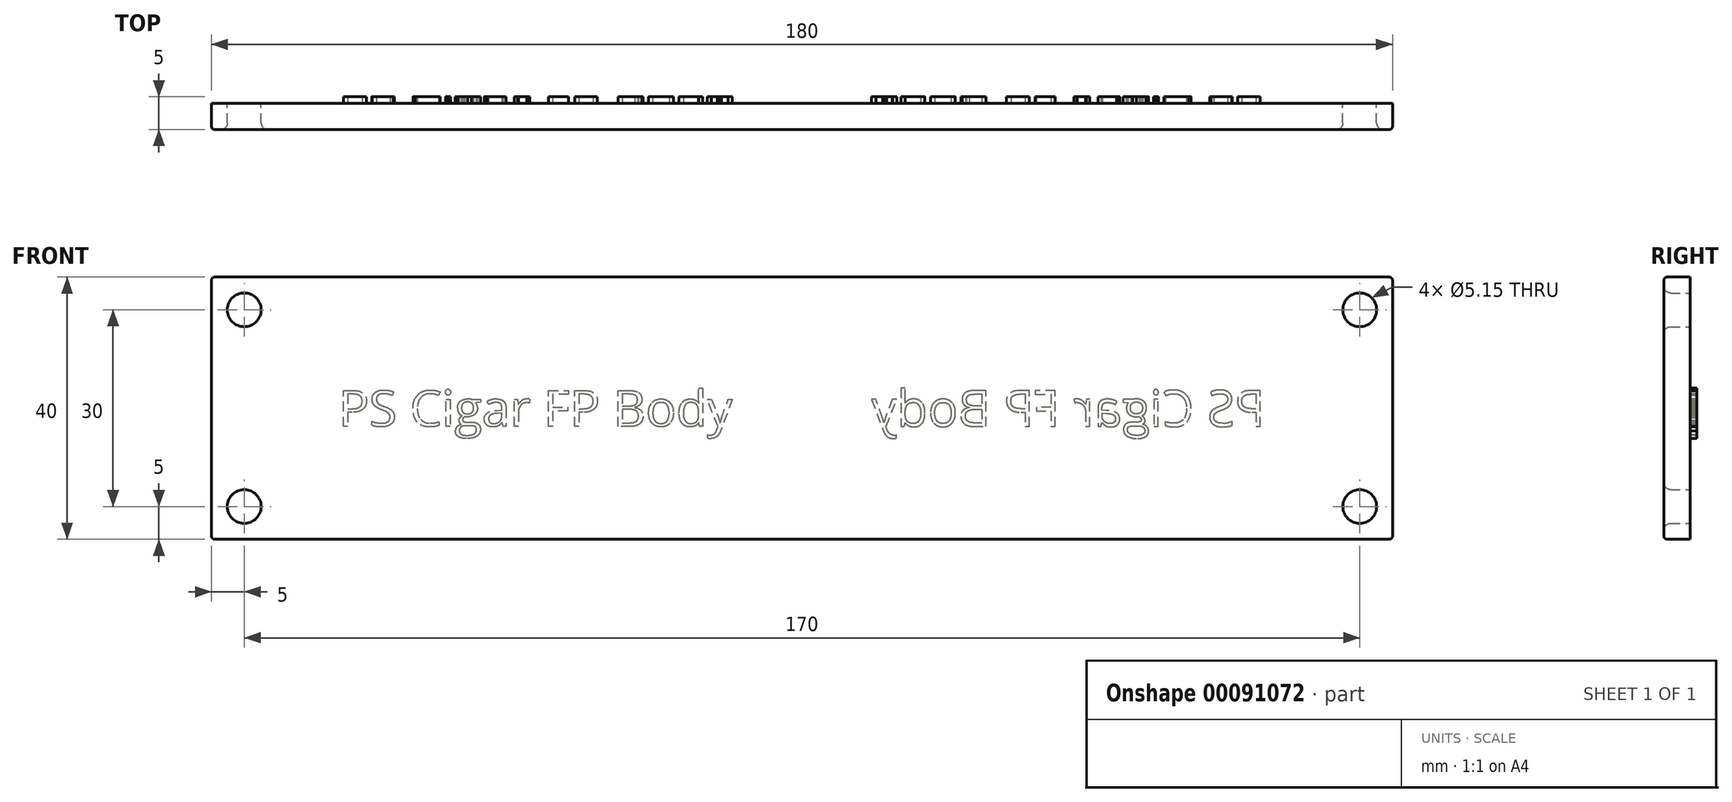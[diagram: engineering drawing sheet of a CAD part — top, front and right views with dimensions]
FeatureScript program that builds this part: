
annotation { "Feature Type Name" : "Feature", "Feature Type Description" : "" }
export const myFeature = defineFeature(function(context is Context, id is Id, definition is map)
    precondition{}
    {
        {
            var Q0;
            Q0=qCreatedBy(makeId("Front.planeOp"),FACE);
            var sketch = newSketch(context, id + "F0", { "sketchPlane" : qUnion([Q0])});
            skLineSegment(sketch, "E0.bottom", {"start": v(-90, -20) * mm, "end": v(90, -20) * mm});
            skLineSegment(sketch, "E0.top", {"start": v(-90, 20) * mm, "end": v(90, 20) * mm});
            skLineSegment(sketch, "E0.left", {"start": v(-90, -20) * mm, "end": v(-90, 20) * mm});
            skLineSegment(sketch, "E0.right", {"start": v(90, -20) * mm, "end": v(90, 20) * mm});
            skPoint(sketch, "E0.middle", {"position": v(0, 0) * mm});
            skCircle(sketch, "E1", {"center": v(-85, 15) * mm, "radius": 2.58 * mm});
            skPoint(sketch, "E2.start.orphan", {"position": v(-90, 0) * mm});
            skPoint(sketch, "E3.orphan", {"position": v(0, 20) * mm});
            skPoint(sketch, "E4.end.orphan", {"position": v(0, -20) * mm});
            skLineSegment(sketch, "E5", {"start": v(-90, 0) * mm, "end": v(0, 0) * mm, "construction": true});
            skLineSegment(sketch, "E6", {"start": v(0, 20) * mm, "end": v(0, -20) * mm, "construction": true});
            skCircle(sketch, "E7.MirrorC", {"center": v(-85, -15) * mm, "radius": 2.58 * mm});
            skCircle(sketch, "E8.MirrorC", {"center": v(85, 15) * mm, "radius": 2.58 * mm});
            skCircle(sketch, "E9.MirrorC", {"center": v(85, -15) * mm, "radius": 2.58 * mm});
            skSolve(sketch);
        }
        {
            var Q0;
            Q0=makeQuery(id+"F0.imprint","IMPRINT",FACE,{"disambiguationData":[TD([[makeQuery(id+"F0.imprint","IMPRINT",EDGE,{"derivedFrom":sQuery(id+"F0.wireOp",EDGE,"E0.bottom")}),1.0]])]});
            extrude(context, id + "F1", {"entities" : qUnion([Q0]), "depth" : 4 * mm});
        }
        {
            var Q0;
            Q0=makeQuery(id+"F1.opExtrude","CAP_EDGE",EDGE,{"disambiguationData":[OSD([sQuery(id+"F0.wireOp",EDGE,"E1")])],"isStart":false});
            var Q1;
            Q1=makeQuery(id+"F1.opExtrude","CAP_EDGE",EDGE,{"disambiguationData":[OSD([sQuery(id+"F0.wireOp",EDGE,"f5b72a5b-8583-449a-bdbf-9ac5a681e1fd0.MirrorC")])],"isStart":false});
            var Q2;
            Q2=makeQuery(id+"F1.opExtrude","CAP_EDGE",EDGE,{"disambiguationData":[OSD([sQuery(id+"F0.wireOp",EDGE,"2623e306-60f4-4522-aa65-1e3e8c2cf5b60.MirrorC")])],"isStart":false});
            var Q3;
            Q3=makeQuery(id+"F1.opExtrude","CAP_EDGE",EDGE,{"disambiguationData":[OSD([sQuery(id+"F0.wireOp",EDGE,"be81a34d-1d50-4ce7-a7a8-4484a1701fac0.MirrorC")])],"isStart":false});
            var Q4;
            Q4=makeQuery(id+"F1.opExtrude","CAP_EDGE",EDGE,{"disambiguationData":[OSD([sQuery(id+"F0.wireOp",EDGE,"E7.MirrorC")])],"isStart":false});
            var Q5;
            Q5=makeQuery(id+"F1.opExtrude","CAP_EDGE",EDGE,{"disambiguationData":[OSD([sQuery(id+"F0.wireOp",EDGE,"E8.MirrorC")])],"isStart":false});
            var Q6;
            Q6=makeQuery(id+"F1.opExtrude","CAP_EDGE",EDGE,{"disambiguationData":[OSD([sQuery(id+"F0.wireOp",EDGE,"E9.MirrorC")])],"isStart":false});
            fillet(context, id + "F2", {"entities" : qUnion([Q0, Q1, Q2, Q3, Q4, Q5, Q6]), "radius" : 1 * mm, "tangentPropagation" : true, "allowEdgeOverflow" : false});
        }
        {
            var Q0;
            Q0=makeQuery(id+"F1.opExtrude","CAP_EDGE",EDGE,{"disambiguationData":[OSD([sQuery(id+"F0.wireOp",EDGE,"E0.top")])],"isStart":false});
            var Q1;
            Q1=makeQuery(id+"F1.opExtrude","CAP_EDGE",EDGE,{"disambiguationData":[OSD([sQuery(id+"F0.wireOp",EDGE,"E0.left")])],"isStart":false});
            var Q2;
            Q2=makeQuery(id+"F1.opExtrude","CAP_EDGE",EDGE,{"disambiguationData":[OSD([sQuery(id+"F0.wireOp",EDGE,"E0.bottom")])],"isStart":false});
            var Q3;
            Q3=makeQuery(id+"F1.opExtrude","CAP_EDGE",EDGE,{"disambiguationData":[OSD([sQuery(id+"F0.wireOp",EDGE,"E0.right")])],"isStart":false});
            var Q4;
            Q4=makeQuery(id+"F1.opExtrude","SWEPT_EDGE",EDGE,{"disambiguationData":[OSD([sQuery(id+"F0.wireOp",EDGE,"E0.top"),sQuery(id+"F0.wireOp",EDGE,"E0.left")])]});
            var Q5;
            Q5=makeQuery(id+"F1.opExtrude","SWEPT_EDGE",EDGE,{"disambiguationData":[OSD([sQuery(id+"F0.wireOp",EDGE,"E0.bottom"),sQuery(id+"F0.wireOp",EDGE,"E0.left")])]});
            var Q6;
            Q6=makeQuery(id+"F1.opExtrude","SWEPT_EDGE",EDGE,{"disambiguationData":[OSD([sQuery(id+"F0.wireOp",EDGE,"E0.top"),sQuery(id+"F0.wireOp",EDGE,"E0.right")])]});
            var Q7;
            Q7=makeQuery(id+"F1.opExtrude","SWEPT_EDGE",EDGE,{"disambiguationData":[OSD([sQuery(id+"F0.wireOp",EDGE,"E0.bottom"),sQuery(id+"F0.wireOp",EDGE,"E0.right")])]});
            fillet(context, id + "F3", {"entities" : qUnion([Q0, Q1, Q2, Q3, Q4, Q5, Q6, Q7]), "radius" : .5 * mm, "tangentPropagation" : true, "allowEdgeOverflow" : false});
        }
        {
            var Q0;
            Q0=makeQuery(id+"F1.opExtrude","CAP_FACE",FACE,{"disambiguationData":[OSD([sQuery(id+"F0.wireOp",EDGE,"E0.bottom"),sQuery(id+"F0.wireOp",EDGE,"E0.top"),sQuery(id+"F0.wireOp",EDGE,"E0.left"),sQuery(id+"F0.wireOp",EDGE,"E0.right"),sQuery(id+"F0.wireOp",EDGE,"E1"),sQuery(id+"F0.wireOp",EDGE,"E7.MirrorC"),sQuery(id+"F0.wireOp",EDGE,"E8.MirrorC"),sQuery(id+"F0.wireOp",EDGE,"E9.MirrorC")])],"isStart":true});
            var sketch = newSketch(context, id + "F4", { "sketchPlane" : qUnion([Q0])});
            skText(sketch, "E10", { "text": "PS Cigar FP Body", "fontName": "OpenSans-Regular.ttf"});
            skLineSegment(sketch, "E11", {"start": v(0, 20) * mm, "end": v(0, -20) * mm, "construction": true});
            const initialGuessF4  = {"E10": [-0.0706, -0.00278, 1, 0, 0.00553]};
            skSetInitialGuess(sketch, initialGuessF4);
            skSolve(sketch);
        }
        {
            var Q0;
            Q0=qSketchRegion(id+"F4",true);
            extrude(context, id + "F5", {"entities" : qUnion([Q0]), "operationType" : NewBodyOperationType.ADD, "depth" : 1 * mm});
        }
        {
            var Q0;
            Q0=makeQuery(id+"F1.opExtrude","SWEPT_BODY",BODY,{"disambiguationData":[OSD([sQuery(id+"F0.wireOp",EDGE,"E0.bottom"),sQuery(id+"F0.wireOp",EDGE,"E0.top"),sQuery(id+"F0.wireOp",EDGE,"E0.left"),sQuery(id+"F0.wireOp",EDGE,"E0.right"),sQuery(id+"F0.wireOp",EDGE,"E1"),sQuery(id+"F0.wireOp",EDGE,"E7.MirrorC"),sQuery(id+"F0.wireOp",EDGE,"E8.MirrorC"),sQuery(id+"F0.wireOp",EDGE,"E9.MirrorC")])]});
            var Q1;
            Q1=makeQuery(id+"F5.opExtrude","SWEPT_FACE",FACE,{"disambiguationData":[OSD([sQuery(id+"F4.wireOp",EDGE,"E10.sketch_text.stroke-94")])]});
            var Q2;
            Q2=makeQuery(id+"F5.opExtrude","SWEPT_FACE",FACE,{"disambiguationData":[OSD([sQuery(id+"F4.wireOp",EDGE,"E10.sketch_text.stroke-169")])]});
            var Q3;
            Q3=makeQuery(id+"F5.opExtrude","SWEPT_FACE",FACE,{"disambiguationData":[OSD([sQuery(id+"F4.wireOp",EDGE,"E10.sketch_text.stroke-185")])]});
            var Q4;
            Q4=makeQuery(id+"F5.opExtrude","SWEPT_FACE",FACE,{"disambiguationData":[OSD([sQuery(id+"F4.wireOp",EDGE,"E10.sketch_text.stroke-125")])]});
            var Q5;
            Q5=makeQuery(id+"F5.opExtrude","SWEPT_FACE",FACE,{"disambiguationData":[OSD([sQuery(id+"F4.wireOp",EDGE,"E10.sketch_text.stroke-155")])]});
            var Q6;
            Q6=makeQuery(id+"F5.opExtrude","SWEPT_FACE",FACE,{"disambiguationData":[OSD([sQuery(id+"F4.wireOp",EDGE,"E10.sketch_text.stroke-65")])]});
            var Q7;
            Q7=makeQuery(id+"F5.opExtrude","SWEPT_FACE",FACE,{"disambiguationData":[OSD([sQuery(id+"F4.wireOp",EDGE,"E10.sketch_text.stroke-81")])]});
            var Q8;
            Q8=makeQuery(id+"F5.opExtrude","SWEPT_FACE",FACE,{"disambiguationData":[OSD([sQuery(id+"F4.wireOp",EDGE,"E10.sketch_text.stroke-67")])]});
            var Q9;
            Q9=makeQuery(id+"F5.opExtrude","SWEPT_FACE",FACE,{"disambiguationData":[OSD([sQuery(id+"F4.wireOp",EDGE,"E10.sketch_text.stroke-99")])]});
            var Q10;
            Q10=makeQuery(id+"F5.opExtrude","SWEPT_FACE",FACE,{"disambiguationData":[OSD([sQuery(id+"F4.wireOp",EDGE,"E10.sketch_text.stroke-127")])]});
            var Q11;
            Q11=makeQuery(id+"F5.opExtrude","SWEPT_FACE",FACE,{"disambiguationData":[OSD([sQuery(id+"F4.wireOp",EDGE,"E10.sketch_text.stroke-10")])]});
            var Q12;
            Q12=makeQuery(id+"F5.opExtrude","CAP_FACE",FACE,{"disambiguationData":[OSD([sQuery(id+"F4.wireOp",EDGE,"E10.sketch_text.stroke-9"),sQuery(id+"F4.wireOp",EDGE,"E10.sketch_text.stroke-10"),sQuery(id+"F4.wireOp",EDGE,"E10.sketch_text.stroke-11"),sQuery(id+"F4.wireOp",EDGE,"E10.sketch_text.stroke-12")])],"isStart":false});
            var Q13;
            Q13=makeQuery(id+"F5.opExtrude","SWEPT_FACE",FACE,{"disambiguationData":[OSD([sQuery(id+"F4.wireOp",EDGE,"E10.sketch_text.stroke-154")])]});
            var Q14;
            Q14=makeQuery(id+"F5.opExtrude","SWEPT_FACE",FACE,{"disambiguationData":[OSD([sQuery(id+"F4.wireOp",EDGE,"E10.sketch_text.stroke-1")])]});
            var Q15;
            Q15=makeQuery(id+"F5.opExtrude","CAP_FACE",FACE,{"disambiguationData":[OSD([sQuery(id+"F4.wireOp",EDGE,"E10.sketch_text.stroke-124"),sQuery(id+"F4.wireOp",EDGE,"E10.sketch_text.stroke-125"),sQuery(id+"F4.wireOp",EDGE,"E10.sketch_text.stroke-126"),sQuery(id+"F4.wireOp",EDGE,"E10.sketch_text.stroke-127"),sQuery(id+"F4.wireOp",EDGE,"E10.sketch_text.stroke-128"),sQuery(id+"F4.wireOp",EDGE,"E10.sketch_text.stroke-129"),sQuery(id+"F4.wireOp",EDGE,"E10.sketch_text.stroke-130"),sQuery(id+"F4.wireOp",EDGE,"E10.sketch_text.stroke-131"),sQuery(id+"F4.wireOp",EDGE,"E10.sketch_text.stroke-132"),sQuery(id+"F4.wireOp",EDGE,"E10.sketch_text.stroke-133"),sQuery(id+"F4.wireOp",EDGE,"E10.sketch_text.stroke-134"),sQuery(id+"F4.wireOp",EDGE,"E10.sketch_text.stroke-135"),sQuery(id+"F4.wireOp",EDGE,"E10.sketch_text.stroke-136"),sQuery(id+"F4.wireOp",EDGE,"E10.sketch_text.stroke-137"),sQuery(id+"F4.wireOp",EDGE,"E10.sketch_text.stroke-138")])],"isStart":false});
            var Q16;
            Q16=makeQuery(id+"F5.opExtrude","CAP_FACE",FACE,{"disambiguationData":[OSD([sQuery(id+"F4.wireOp",EDGE,"E10.sketch_text.stroke-34"),sQuery(id+"F4.wireOp",EDGE,"E10.sketch_text.stroke-35"),sQuery(id+"F4.wireOp",EDGE,"E10.sketch_text.stroke-36"),sQuery(id+"F4.wireOp",EDGE,"E10.sketch_text.stroke-37"),sQuery(id+"F4.wireOp",EDGE,"E10.sketch_text.stroke-38"),sQuery(id+"F4.wireOp",EDGE,"E10.sketch_text.stroke-39"),sQuery(id+"F4.wireOp",EDGE,"E10.sketch_text.stroke-40"),sQuery(id+"F4.wireOp",EDGE,"E10.sketch_text.stroke-41"),sQuery(id+"F4.wireOp",EDGE,"E10.sketch_text.stroke-42"),sQuery(id+"F4.wireOp",EDGE,"E10.sketch_text.stroke-43"),sQuery(id+"F4.wireOp",EDGE,"E10.sketch_text.stroke-44"),sQuery(id+"F4.wireOp",EDGE,"E10.sketch_text.stroke-45"),sQuery(id+"F4.wireOp",EDGE,"E10.sketch_text.stroke-46"),sQuery(id+"F4.wireOp",EDGE,"E10.sketch_text.stroke-47"),sQuery(id+"F4.wireOp",EDGE,"E10.sketch_text.stroke-48"),sQuery(id+"F4.wireOp",EDGE,"E10.sketch_text.stroke-49"),sQuery(id+"F4.wireOp",EDGE,"E10.sketch_text.stroke-50"),sQuery(id+"F4.wireOp",EDGE,"E10.sketch_text.stroke-51"),sQuery(id+"F4.wireOp",EDGE,"E10.sketch_text.stroke-52"),sQuery(id+"F4.wireOp",EDGE,"E10.sketch_text.stroke-53"),sQuery(id+"F4.wireOp",EDGE,"E10.sketch_text.stroke-54"),sQuery(id+"F4.wireOp",EDGE,"E10.sketch_text.stroke-55"),sQuery(id+"F4.wireOp",EDGE,"E10.sketch_text.stroke-56"),sQuery(id+"F4.wireOp",EDGE,"E10.sketch_text.stroke-57"),sQuery(id+"F4.wireOp",EDGE,"E10.sketch_text.stroke-58"),sQuery(id+"F4.wireOp",EDGE,"E10.sketch_text.stroke-59"),sQuery(id+"F4.wireOp",EDGE,"E10.sketch_text.stroke-60")])],"isStart":false});
            var Q17;
            Q17=makeQuery(id+"F5.opExtrude","SWEPT_FACE",FACE,{"disambiguationData":[OSD([sQuery(id+"F4.wireOp",EDGE,"E10.sketch_text.stroke-50")])]});
            var Q18;
            Q18=makeQuery(id+"F5.opExtrude","SWEPT_FACE",FACE,{"disambiguationData":[OSD([sQuery(id+"F4.wireOp",EDGE,"E10.sketch_text.stroke-2")])]});
            var Q19;
            Q19=makeQuery(id+"F5.opExtrude","SWEPT_FACE",FACE,{"disambiguationData":[OSD([sQuery(id+"F4.wireOp",EDGE,"E10.sketch_text.stroke-3")])]});
            var Q20;
            Q20=makeQuery(id+"F5.opExtrude","SWEPT_FACE",FACE,{"disambiguationData":[OSD([sQuery(id+"F4.wireOp",EDGE,"E10.sketch_text.stroke-5")])]});
            var Q21;
            Q21=makeQuery(id+"F5.opExtrude","SWEPT_FACE",FACE,{"disambiguationData":[OSD([sQuery(id+"F4.wireOp",EDGE,"E10.sketch_text.stroke-8")])]});
            var Q22;
            Q22=makeQuery(id+"F5.opExtrude","SWEPT_FACE",FACE,{"disambiguationData":[OSD([sQuery(id+"F4.wireOp",EDGE,"E10.sketch_text.stroke-98")])]});
            var Q23;
            Q23=makeQuery(id+"F5.opExtrude","SWEPT_FACE",FACE,{"disambiguationData":[OSD([sQuery(id+"F4.wireOp",EDGE,"E10.sketch_text.stroke-66")])]});
            var Q24;
            Q24=makeQuery(id+"F5.opExtrude","SWEPT_FACE",FACE,{"disambiguationData":[OSD([sQuery(id+"F4.wireOp",EDGE,"E10.sketch_text.stroke-153")])]});
            var Q25;
            Q25=makeQuery(id+"F5.opExtrude","SWEPT_FACE",FACE,{"disambiguationData":[OSD([sQuery(id+"F4.wireOp",EDGE,"E10.sketch_text.stroke-126")])]});
            var Q26;
            Q26=makeQuery(id+"F5.opExtrude","SWEPT_FACE",FACE,{"disambiguationData":[OSD([sQuery(id+"F4.wireOp",EDGE,"E10.sketch_text.stroke-183")])]});
            var Q27;
            Q27=makeQuery(id+"F5.opExtrude","SWEPT_FACE",FACE,{"disambiguationData":[OSD([sQuery(id+"F4.wireOp",EDGE,"E10.sketch_text.stroke-109")])]});
            var Q28;
            Q28=makeQuery(id+"F5.opExtrude","SWEPT_FACE",FACE,{"disambiguationData":[OSD([sQuery(id+"F4.wireOp",EDGE,"E10.sketch_text.stroke-186")])]});
            var Q29;
            Q29=makeQuery(id+"F5.opExtrude","SWEPT_FACE",FACE,{"disambiguationData":[OSD([sQuery(id+"F4.wireOp",EDGE,"E10.sketch_text.stroke-79")])]});
            var Q30;
            Q30=makeQuery(id+"F5.opExtrude","SWEPT_FACE",FACE,{"disambiguationData":[OSD([sQuery(id+"F4.wireOp",EDGE,"E10.sketch_text.stroke-110")])]});
            var Q31;
            Q31=makeQuery(id+"F5.opExtrude","SWEPT_FACE",FACE,{"disambiguationData":[OSD([sQuery(id+"F4.wireOp",EDGE,"E10.sketch_text.stroke-38")])]});
            var Q32;
            Q32=makeQuery(id+"F5.opExtrude","SWEPT_FACE",FACE,{"disambiguationData":[OSD([sQuery(id+"F4.wireOp",EDGE,"E10.sketch_text.stroke-24")])]});
            var Q33;
            Q33=makeQuery(id+"F5.opExtrude","SWEPT_FACE",FACE,{"disambiguationData":[OSD([sQuery(id+"F4.wireOp",EDGE,"E10.sketch_text.stroke-12")])]});
            var Q34;
            Q34=makeQuery(id+"F5.opExtrude","SWEPT_FACE",FACE,{"disambiguationData":[OSD([sQuery(id+"F4.wireOp",EDGE,"E10.sketch_text.stroke-100")])]});
            var Q35;
            Q35=makeQuery(id+"F5.opExtrude","SWEPT_FACE",FACE,{"disambiguationData":[OSD([sQuery(id+"F4.wireOp",EDGE,"E10.sketch_text.stroke-158")])]});
            var Q36;
            Q36=makeQuery(id+"F5.opExtrude","SWEPT_FACE",FACE,{"disambiguationData":[OSD([sQuery(id+"F4.wireOp",EDGE,"E10.sketch_text.stroke-142")])]});
            var Q37;
            Q37=makeQuery(id+"F5.opExtrude","SWEPT_FACE",FACE,{"disambiguationData":[OSD([sQuery(id+"F4.wireOp",EDGE,"E10.sketch_text.stroke-54")])]});
            var Q38;
            Q38=makeQuery(id+"F5.opExtrude","SWEPT_FACE",FACE,{"disambiguationData":[OSD([sQuery(id+"F4.wireOp",EDGE,"E10.sketch_text.stroke-25")])]});
            var Q39;
            Q39=makeQuery(id+"F5.opExtrude","SWEPT_FACE",FACE,{"disambiguationData":[OSD([sQuery(id+"F4.wireOp",EDGE,"E10.sketch_text.stroke-101")])]});
            var Q40;
            Q40=makeQuery(id+"F5.opExtrude","SWEPT_FACE",FACE,{"disambiguationData":[OSD([sQuery(id+"F4.wireOp",EDGE,"E10.sketch_text.stroke-69")])]});
            var Q41;
            Q41=makeQuery(id+"F5.opExtrude","SWEPT_FACE",FACE,{"disambiguationData":[OSD([sQuery(id+"F4.wireOp",EDGE,"E10.sketch_text.stroke-159")])]});
            var Q42;
            Q42=makeQuery(id+"F5.opExtrude","SWEPT_FACE",FACE,{"disambiguationData":[OSD([sQuery(id+"F4.wireOp",EDGE,"E10.sketch_text.stroke-85")])]});
            var Q43;
            Q43=makeQuery(id+"F5.opExtrude","SWEPT_FACE",FACE,{"disambiguationData":[OSD([sQuery(id+"F4.wireOp",EDGE,"E10.sketch_text.stroke-173")])]});
            var Q44;
            Q44=makeQuery(id+"F5.opExtrude","SWEPT_FACE",FACE,{"disambiguationData":[OSD([sQuery(id+"F4.wireOp",EDGE,"E10.sketch_text.stroke-40")])]});
            var Q45;
            Q45=makeQuery(id+"F5.opExtrude","SWEPT_FACE",FACE,{"disambiguationData":[OSD([sQuery(id+"F4.wireOp",EDGE,"E10.sketch_text.stroke-102")])]});
            var Q46;
            Q46=makeQuery(id+"F5.opExtrude","SWEPT_FACE",FACE,{"disambiguationData":[OSD([sQuery(id+"F4.wireOp",EDGE,"E10.sketch_text.stroke-86")])]});
            var Q47;
            Q47=makeQuery(id+"F5.opExtrude","SWEPT_FACE",FACE,{"disambiguationData":[OSD([sQuery(id+"F4.wireOp",EDGE,"E10.sketch_text.stroke-130")])]});
            var Q48;
            Q48=makeQuery(id+"F5.opExtrude","SWEPT_FACE",FACE,{"disambiguationData":[OSD([sQuery(id+"F4.wireOp",EDGE,"E10.sketch_text.stroke-103")])]});
            var Q49;
            Q49=makeQuery(id+"F5.opExtrude","SWEPT_FACE",FACE,{"disambiguationData":[OSD([sQuery(id+"F4.wireOp",EDGE,"E10.sketch_text.stroke-87")])]});
            var Q50;
            Q50=makeQuery(id+"F5.opExtrude","SWEPT_FACE",FACE,{"disambiguationData":[OSD([sQuery(id+"F4.wireOp",EDGE,"E10.sketch_text.stroke-145")])]});
            var Q51;
            Q51=makeQuery(id+"F5.opExtrude","SWEPT_FACE",FACE,{"disambiguationData":[OSD([sQuery(id+"F4.wireOp",EDGE,"E10.sketch_text.stroke-131")])]});
            var Q52;
            Q52=makeQuery(id+"F5.opExtrude","SWEPT_FACE",FACE,{"disambiguationData":[OSD([sQuery(id+"F4.wireOp",EDGE,"E10.sketch_text.stroke-28")])]});
            var Q53;
            Q53=makeQuery(id+"F5.opExtrude","SWEPT_FACE",FACE,{"disambiguationData":[OSD([sQuery(id+"F4.wireOp",EDGE,"E10.sketch_text.stroke-14")])]});
            var Q54;
            Q54=makeQuery(id+"F5.opExtrude","SWEPT_FACE",FACE,{"disambiguationData":[OSD([sQuery(id+"F4.wireOp",EDGE,"E10.sketch_text.stroke-88")])]});
            var Q55;
            Q55=makeQuery(id+"F5.opExtrude","SWEPT_FACE",FACE,{"disambiguationData":[OSD([sQuery(id+"F4.wireOp",EDGE,"E10.sketch_text.stroke-162")])]});
            var Q56;
            Q56=makeQuery(id+"F5.opExtrude","SWEPT_FACE",FACE,{"disambiguationData":[OSD([sQuery(id+"F4.wireOp",EDGE,"E10.sketch_text.stroke-176")])]});
            var Q57;
            Q57=makeQuery(id+"F5.opExtrude","SWEPT_FACE",FACE,{"disambiguationData":[OSD([sQuery(id+"F4.wireOp",EDGE,"E10.sketch_text.stroke-73")])]});
            var Q58;
            Q58=makeQuery(id+"F5.opExtrude","SWEPT_FACE",FACE,{"disambiguationData":[OSD([sQuery(id+"F4.wireOp",EDGE,"E10.sketch_text.stroke-59")])]});
            var Q59;
            Q59=makeQuery(id+"F5.opExtrude","SWEPT_FACE",FACE,{"disambiguationData":[OSD([sQuery(id+"F4.wireOp",EDGE,"E10.sketch_text.stroke-133")])]});
            var Q60;
            Q60=makeQuery(id+"F5.opExtrude","SWEPT_FACE",FACE,{"disambiguationData":[OSD([sQuery(id+"F4.wireOp",EDGE,"E10.sketch_text.stroke-119")])]});
            var Q61;
            Q61=makeQuery(id+"F5.opExtrude","SWEPT_FACE",FACE,{"disambiguationData":[OSD([sQuery(id+"F4.wireOp",EDGE,"E10.sketch_text.stroke-74")])]});
            var Q62;
            Q62=makeQuery(id+"F5.opExtrude","SWEPT_FACE",FACE,{"disambiguationData":[OSD([sQuery(id+"F4.wireOp",EDGE,"E10.sketch_text.stroke-44")])]});
            var Q63;
            Q63=makeQuery(id+"F5.opExtrude","SWEPT_FACE",FACE,{"disambiguationData":[OSD([sQuery(id+"F4.wireOp",EDGE,"E10.sketch_text.stroke-120")])]});
            var Q64;
            Q64=makeQuery(id+"F5.opExtrude","SWEPT_FACE",FACE,{"disambiguationData":[OSD([sQuery(id+"F4.wireOp",EDGE,"E10.sketch_text.stroke-90")])]});
            var Q65;
            Q65=makeQuery(id+"F5.opExtrude","SWEPT_FACE",FACE,{"disambiguationData":[OSD([sQuery(id+"F4.wireOp",EDGE,"E10.sketch_text.stroke-178")])]});
            var Q66;
            Q66=makeQuery(id+"F5.opExtrude","SWEPT_FACE",FACE,{"disambiguationData":[OSD([sQuery(id+"F4.wireOp",EDGE,"E10.sketch_text.stroke-45")])]});
            var Q67;
            Q67=makeQuery(id+"F5.opExtrude","SWEPT_FACE",FACE,{"disambiguationData":[OSD([sQuery(id+"F4.wireOp",EDGE,"E10.sketch_text.stroke-31")])]});
            var Q68;
            Q68=makeQuery(id+"F5.opExtrude","SWEPT_FACE",FACE,{"disambiguationData":[OSD([sQuery(id+"F4.wireOp",EDGE,"E10.sketch_text.stroke-135")])]});
            var Q69;
            Q69=makeQuery(id+"F5.opExtrude","SWEPT_FACE",FACE,{"disambiguationData":[OSD([sQuery(id+"F4.wireOp",EDGE,"E10.sketch_text.stroke-179")])]});
            var Q70;
            Q70=makeQuery(id+"F5.opExtrude","SWEPT_FACE",FACE,{"disambiguationData":[OSD([sQuery(id+"F4.wireOp",EDGE,"E10.sketch_text.stroke-165")])]});
            var Q71;
            Q71=makeQuery(id+"F5.opExtrude","SWEPT_FACE",FACE,{"disambiguationData":[OSD([sQuery(id+"F4.wireOp",EDGE,"E10.sketch_text.stroke-149")])]});
            var Q72;
            Q72=makeQuery(id+"F5.opExtrude","SWEPT_FACE",FACE,{"disambiguationData":[OSD([sQuery(id+"F4.wireOp",EDGE,"E10.sketch_text.stroke-136")])]});
            var Q73;
            Q73=makeQuery(id+"F5.opExtrude","SWEPT_FACE",FACE,{"disambiguationData":[OSD([sQuery(id+"F4.wireOp",EDGE,"E10.sketch_text.stroke-122")])]});
            var Q74;
            Q74=makeQuery(id+"F5.opExtrude","SWEPT_FACE",FACE,{"disambiguationData":[OSD([sQuery(id+"F4.wireOp",EDGE,"E10.sketch_text.stroke-106")])]});
            var Q75;
            Q75=makeQuery(id+"F5.opExtrude","SWEPT_FACE",FACE,{"disambiguationData":[OSD([sQuery(id+"F4.wireOp",EDGE,"E10.sketch_text.stroke-180")])]});
            var Q76;
            Q76=makeQuery(id+"F5.opExtrude","SWEPT_FACE",FACE,{"disambiguationData":[OSD([sQuery(id+"F4.wireOp",EDGE,"E10.sketch_text.stroke-166")])]});
            var Q77;
            Q77=makeQuery(id+"F5.opExtrude","SWEPT_FACE",FACE,{"disambiguationData":[OSD([sQuery(id+"F4.wireOp",EDGE,"E10.sketch_text.stroke-150")])]});
            var Q78;
            Q78=makeQuery(id+"F5.opExtrude","SWEPT_FACE",FACE,{"disambiguationData":[OSD([sQuery(id+"F4.wireOp",EDGE,"E10.sketch_text.stroke-76")])]});
            var Q79;
            Q79=makeQuery(id+"F5.opExtrude","SWEPT_FACE",FACE,{"disambiguationData":[OSD([sQuery(id+"F4.wireOp",EDGE,"E10.sketch_text.stroke-32")])]});
            var Q80;
            Q80=makeQuery(id+"F5.opExtrude","SWEPT_FACE",FACE,{"disambiguationData":[OSD([sQuery(id+"F4.wireOp",EDGE,"E10.sketch_text.stroke-181")])]});
            var Q81;
            Q81=makeQuery(id+"F5.opExtrude","SWEPT_FACE",FACE,{"disambiguationData":[OSD([sQuery(id+"F4.wireOp",EDGE,"E10.sketch_text.stroke-47")])]});
            var Q82;
            Q82=makeQuery(id+"F5.opExtrude","SWEPT_FACE",FACE,{"disambiguationData":[OSD([sQuery(id+"F4.wireOp",EDGE,"E10.sketch_text.stroke-123")])]});
            var Q83;
            Q83=makeQuery(id+"F5.opExtrude","SWEPT_FACE",FACE,{"disambiguationData":[OSD([sQuery(id+"F4.wireOp",EDGE,"E10.sketch_text.stroke-107")])]});
            var Q84;
            Q84=makeQuery(id+"F5.opExtrude","SWEPT_FACE",FACE,{"disambiguationData":[OSD([sQuery(id+"F4.wireOp",EDGE,"E10.sketch_text.stroke-48")])]});
            var Q85;
            Q85=makeQuery(id+"F5.opExtrude","SWEPT_FACE",FACE,{"disambiguationData":[OSD([sQuery(id+"F4.wireOp",EDGE,"E10.sketch_text.stroke-124")])]});
            var Q86;
            Q86=makeQuery(id+"F5.opExtrude","SWEPT_FACE",FACE,{"disambiguationData":[OSD([sQuery(id+"F4.wireOp",EDGE,"E10.sketch_text.stroke-108")])]});
            var Q87;
            Q87=makeQuery(id+"F5.opExtrude","CAP_FACE",FACE,{"disambiguationData":[OSD([sQuery(id+"F4.wireOp",EDGE,"E10.sketch_text.stroke-139"),sQuery(id+"F4.wireOp",EDGE,"E10.sketch_text.stroke-140"),sQuery(id+"F4.wireOp",EDGE,"E10.sketch_text.stroke-141"),sQuery(id+"F4.wireOp",EDGE,"E10.sketch_text.stroke-142"),sQuery(id+"F4.wireOp",EDGE,"E10.sketch_text.stroke-143"),sQuery(id+"F4.wireOp",EDGE,"E10.sketch_text.stroke-144"),sQuery(id+"F4.wireOp",EDGE,"E10.sketch_text.stroke-145"),sQuery(id+"F4.wireOp",EDGE,"E10.sketch_text.stroke-146"),sQuery(id+"F4.wireOp",EDGE,"E10.sketch_text.stroke-147"),sQuery(id+"F4.wireOp",EDGE,"E10.sketch_text.stroke-148"),sQuery(id+"F4.wireOp",EDGE,"E10.sketch_text.stroke-149"),sQuery(id+"F4.wireOp",EDGE,"E10.sketch_text.stroke-150"),sQuery(id+"F4.wireOp",EDGE,"E10.sketch_text.stroke-151"),sQuery(id+"F4.wireOp",EDGE,"E10.sketch_text.stroke-152"),sQuery(id+"F4.wireOp",EDGE,"E10.sketch_text.stroke-153"),sQuery(id+"F4.wireOp",EDGE,"E10.sketch_text.stroke-154"),sQuery(id+"F4.wireOp",EDGE,"E10.sketch_text.stroke-155"),sQuery(id+"F4.wireOp",EDGE,"E10.sketch_text.stroke-156"),sQuery(id+"F4.wireOp",EDGE,"E10.sketch_text.stroke-157"),sQuery(id+"F4.wireOp",EDGE,"E10.sketch_text.stroke-158"),sQuery(id+"F4.wireOp",EDGE,"E10.sketch_text.stroke-159"),sQuery(id+"F4.wireOp",EDGE,"E10.sketch_text.stroke-160"),sQuery(id+"F4.wireOp",EDGE,"E10.sketch_text.stroke-161"),sQuery(id+"F4.wireOp",EDGE,"E10.sketch_text.stroke-162"),sQuery(id+"F4.wireOp",EDGE,"E10.sketch_text.stroke-163"),sQuery(id+"F4.wireOp",EDGE,"E10.sketch_text.stroke-164"),sQuery(id+"F4.wireOp",EDGE,"E10.sketch_text.stroke-165")])],"isStart":false});
            var Q88;
            Q88=makeQuery(id+"F5.opExtrude","CAP_FACE",FACE,{"disambiguationData":[OSD([sQuery(id+"F4.wireOp",EDGE,"E10.sketch_text.stroke-21"),sQuery(id+"F4.wireOp",EDGE,"E10.sketch_text.stroke-22"),sQuery(id+"F4.wireOp",EDGE,"E10.sketch_text.stroke-23"),sQuery(id+"F4.wireOp",EDGE,"E10.sketch_text.stroke-24"),sQuery(id+"F4.wireOp",EDGE,"E10.sketch_text.stroke-25"),sQuery(id+"F4.wireOp",EDGE,"E10.sketch_text.stroke-26"),sQuery(id+"F4.wireOp",EDGE,"E10.sketch_text.stroke-27"),sQuery(id+"F4.wireOp",EDGE,"E10.sketch_text.stroke-28"),sQuery(id+"F4.wireOp",EDGE,"E10.sketch_text.stroke-29"),sQuery(id+"F4.wireOp",EDGE,"E10.sketch_text.stroke-30"),sQuery(id+"F4.wireOp",EDGE,"E10.sketch_text.stroke-31"),sQuery(id+"F4.wireOp",EDGE,"E10.sketch_text.stroke-32"),sQuery(id+"F4.wireOp",EDGE,"E10.sketch_text.stroke-33")])],"isStart":false});
            var Q89;
            Q89=makeQuery(id+"F5.opExtrude","SWEPT_FACE",FACE,{"disambiguationData":[OSD([sQuery(id+"F4.wireOp",EDGE,"E10.sketch_text.stroke-113")])]});
            var Q90;
            Q90=makeQuery(id+"F5.opExtrude","SWEPT_FACE",FACE,{"disambiguationData":[OSD([sQuery(id+"F4.wireOp",EDGE,"E10.sketch_text.stroke-37")])]});
            var Q91;
            Q91=makeQuery(id+"F5.opExtrude","SWEPT_FACE",FACE,{"disambiguationData":[OSD([sQuery(id+"F4.wireOp",EDGE,"E10.sketch_text.stroke-187")])]});
            var Q92;
            Q92=makeQuery(id+"F5.opExtrude","SWEPT_FACE",FACE,{"disambiguationData":[OSD([sQuery(id+"F4.wireOp",EDGE,"E10.sketch_text.stroke-0")])]});
            var Q93;
            Q93=makeQuery(id+"F5.opExtrude","SWEPT_FACE",FACE,{"disambiguationData":[OSD([sQuery(id+"F4.wireOp",EDGE,"E10.sketch_text.stroke-4")])]});
            var Q94;
            Q94=makeQuery(id+"F5.opExtrude","SWEPT_FACE",FACE,{"disambiguationData":[OSD([sQuery(id+"F4.wireOp",EDGE,"E10.sketch_text.stroke-82")])]});
            var Q95;
            Q95=makeQuery(id+"F5.opExtrude","SWEPT_FACE",FACE,{"disambiguationData":[OSD([sQuery(id+"F4.wireOp",EDGE,"E10.sketch_text.stroke-52")])]});
            var Q96;
            Q96=makeQuery(id+"F5.opExtrude","SWEPT_FACE",FACE,{"disambiguationData":[OSD([sQuery(id+"F4.wireOp",EDGE,"E10.sketch_text.stroke-49")])]});
            var Q97;
            Q97=makeQuery(id+"F5.opExtrude","SWEPT_FACE",FACE,{"disambiguationData":[OSD([sQuery(id+"F4.wireOp",EDGE,"E10.sketch_text.stroke-63")])]});
            var Q98;
            Q98=makeQuery(id+"F5.opExtrude","SWEPT_FACE",FACE,{"disambiguationData":[OSD([sQuery(id+"F4.wireOp",EDGE,"E10.sketch_text.stroke-21")])]});
            var Q99;
            Q99=makeQuery(id+"F5.opExtrude","SWEPT_FACE",FACE,{"disambiguationData":[OSD([sQuery(id+"F4.wireOp",EDGE,"E10.sketch_text.stroke-128")])]});
            var Q100;
            Q100=makeQuery(id+"F5.opExtrude","SWEPT_FACE",FACE,{"disambiguationData":[OSD([sQuery(id+"F4.wireOp",EDGE,"E10.sketch_text.stroke-55")])]});
            var Q101;
            Q101=makeQuery(id+"F5.opExtrude","SWEPT_FACE",FACE,{"disambiguationData":[OSD([sQuery(id+"F4.wireOp",EDGE,"E10.sketch_text.stroke-26")])]});
            var Q102;
            Q102=makeQuery(id+"F5.opExtrude","SWEPT_FACE",FACE,{"disambiguationData":[OSD([sQuery(id+"F4.wireOp",EDGE,"E10.sketch_text.stroke-174")])]});
            var Q103;
            Q103=makeQuery(id+"F5.opExtrude","SWEPT_FACE",FACE,{"disambiguationData":[OSD([sQuery(id+"F4.wireOp",EDGE,"E10.sketch_text.stroke-104")])]});
            var Q104;
            Q104=makeQuery(id+"F5.opExtrude","SWEPT_FACE",FACE,{"disambiguationData":[OSD([sQuery(id+"F4.wireOp",EDGE,"E10.sketch_text.stroke-72")])]});
            var Q105;
            Q105=makeQuery(id+"F5.opExtrude","SWEPT_FACE",FACE,{"disambiguationData":[OSD([sQuery(id+"F4.wireOp",EDGE,"E10.sketch_text.stroke-132")])]});
            var Q106;
            Q106=makeQuery(id+"F5.opExtrude","SWEPT_FACE",FACE,{"disambiguationData":[OSD([sQuery(id+"F4.wireOp",EDGE,"E10.sketch_text.stroke-43")])]});
            var Q107;
            Q107=makeQuery(id+"F5.opExtrude","SWEPT_FACE",FACE,{"disambiguationData":[OSD([sQuery(id+"F4.wireOp",EDGE,"E10.sketch_text.stroke-15")])]});
            var Q108;
            Q108=makeQuery(id+"F5.opExtrude","SWEPT_FACE",FACE,{"disambiguationData":[OSD([sQuery(id+"F4.wireOp",EDGE,"E10.sketch_text.stroke-89")])]});
            var Q109;
            Q109=makeQuery(id+"F5.opExtrude","SWEPT_FACE",FACE,{"disambiguationData":[OSD([sQuery(id+"F4.wireOp",EDGE,"E10.sketch_text.stroke-163")])]});
            var Q110;
            Q110=makeQuery(id+"F5.opExtrude","SWEPT_FACE",FACE,{"disambiguationData":[OSD([sQuery(id+"F4.wireOp",EDGE,"E10.sketch_text.stroke-30")])]});
            var Q111;
            Q111=makeQuery(id+"F5.opExtrude","SWEPT_FACE",FACE,{"disambiguationData":[OSD([sQuery(id+"F4.wireOp",EDGE,"E10.sketch_text.stroke-134")])]});
            var Q112;
            Q112=makeQuery(id+"F5.opExtrude","SWEPT_FACE",FACE,{"disambiguationData":[OSD([sQuery(id+"F4.wireOp",EDGE,"E10.sketch_text.stroke-121")])]});
            var Q113;
            Q113=makeQuery(id+"F5.opExtrude","CAP_FACE",FACE,{"disambiguationData":[OSD([sQuery(id+"F4.wireOp",EDGE,"E10.sketch_text.stroke-105"),sQuery(id+"F4.wireOp",EDGE,"E10.sketch_text.stroke-106"),sQuery(id+"F4.wireOp",EDGE,"E10.sketch_text.stroke-107"),sQuery(id+"F4.wireOp",EDGE,"E10.sketch_text.stroke-108"),sQuery(id+"F4.wireOp",EDGE,"E10.sketch_text.stroke-109"),sQuery(id+"F4.wireOp",EDGE,"E10.sketch_text.stroke-110"),sQuery(id+"F4.wireOp",EDGE,"E10.sketch_text.stroke-111"),sQuery(id+"F4.wireOp",EDGE,"E10.sketch_text.stroke-112"),sQuery(id+"F4.wireOp",EDGE,"E10.sketch_text.stroke-113"),sQuery(id+"F4.wireOp",EDGE,"E10.sketch_text.stroke-114"),sQuery(id+"F4.wireOp",EDGE,"E10.sketch_text.stroke-115"),sQuery(id+"F4.wireOp",EDGE,"E10.sketch_text.stroke-116"),sQuery(id+"F4.wireOp",EDGE,"E10.sketch_text.stroke-117"),sQuery(id+"F4.wireOp",EDGE,"E10.sketch_text.stroke-118"),sQuery(id+"F4.wireOp",EDGE,"E10.sketch_text.stroke-119"),sQuery(id+"F4.wireOp",EDGE,"E10.sketch_text.stroke-120"),sQuery(id+"F4.wireOp",EDGE,"E10.sketch_text.stroke-121"),sQuery(id+"F4.wireOp",EDGE,"E10.sketch_text.stroke-122"),sQuery(id+"F4.wireOp",EDGE,"E10.sketch_text.stroke-123")])],"isStart":false});
            var Q114;
            Q114=makeQuery(id+"F5.opExtrude","SWEPT_FACE",FACE,{"disambiguationData":[OSD([sQuery(id+"F4.wireOp",EDGE,"E10.sketch_text.stroke-92")])]});
            var Q115;
            Q115=makeQuery(id+"F5.opExtrude","SWEPT_FACE",FACE,{"disambiguationData":[OSD([sQuery(id+"F4.wireOp",EDGE,"E10.sketch_text.stroke-46")])]});
            var Q116;
            Q116=makeQuery(id+"F5.opExtrude","CAP_FACE",FACE,{"disambiguationData":[OSD([sQuery(id+"F4.wireOp",EDGE,"E10.sketch_text.stroke-61"),sQuery(id+"F4.wireOp",EDGE,"E10.sketch_text.stroke-62"),sQuery(id+"F4.wireOp",EDGE,"E10.sketch_text.stroke-63"),sQuery(id+"F4.wireOp",EDGE,"E10.sketch_text.stroke-64"),sQuery(id+"F4.wireOp",EDGE,"E10.sketch_text.stroke-65"),sQuery(id+"F4.wireOp",EDGE,"E10.sketch_text.stroke-66"),sQuery(id+"F4.wireOp",EDGE,"E10.sketch_text.stroke-67"),sQuery(id+"F4.wireOp",EDGE,"E10.sketch_text.stroke-68"),sQuery(id+"F4.wireOp",EDGE,"E10.sketch_text.stroke-69"),sQuery(id+"F4.wireOp",EDGE,"E10.sketch_text.stroke-70"),sQuery(id+"F4.wireOp",EDGE,"E10.sketch_text.stroke-71"),sQuery(id+"F4.wireOp",EDGE,"E10.sketch_text.stroke-72"),sQuery(id+"F4.wireOp",EDGE,"E10.sketch_text.stroke-73"),sQuery(id+"F4.wireOp",EDGE,"E10.sketch_text.stroke-74"),sQuery(id+"F4.wireOp",EDGE,"E10.sketch_text.stroke-75"),sQuery(id+"F4.wireOp",EDGE,"E10.sketch_text.stroke-76"),sQuery(id+"F4.wireOp",EDGE,"E10.sketch_text.stroke-77"),sQuery(id+"F4.wireOp",EDGE,"E10.sketch_text.stroke-78"),sQuery(id+"F4.wireOp",EDGE,"E10.sketch_text.stroke-79"),sQuery(id+"F4.wireOp",EDGE,"E10.sketch_text.stroke-80"),sQuery(id+"F4.wireOp",EDGE,"E10.sketch_text.stroke-81"),sQuery(id+"F4.wireOp",EDGE,"E10.sketch_text.stroke-82"),sQuery(id+"F4.wireOp",EDGE,"E10.sketch_text.stroke-83"),sQuery(id+"F4.wireOp",EDGE,"E10.sketch_text.stroke-84"),sQuery(id+"F4.wireOp",EDGE,"E10.sketch_text.stroke-85"),sQuery(id+"F4.wireOp",EDGE,"E10.sketch_text.stroke-86"),sQuery(id+"F4.wireOp",EDGE,"E10.sketch_text.stroke-87"),sQuery(id+"F4.wireOp",EDGE,"E10.sketch_text.stroke-88"),sQuery(id+"F4.wireOp",EDGE,"E10.sketch_text.stroke-89"),sQuery(id+"F4.wireOp",EDGE,"E10.sketch_text.stroke-90"),sQuery(id+"F4.wireOp",EDGE,"E10.sketch_text.stroke-91"),sQuery(id+"F4.wireOp",EDGE,"E10.sketch_text.stroke-92"),sQuery(id+"F4.wireOp",EDGE,"E10.sketch_text.stroke-93"),sQuery(id+"F4.wireOp",EDGE,"E10.sketch_text.stroke-94"),sQuery(id+"F4.wireOp",EDGE,"E10.sketch_text.stroke-95"),sQuery(id+"F4.wireOp",EDGE,"E10.sketch_text.stroke-96"),sQuery(id+"F4.wireOp",EDGE,"E10.sketch_text.stroke-97"),sQuery(id+"F4.wireOp",EDGE,"E10.sketch_text.stroke-98"),sQuery(id+"F4.wireOp",EDGE,"E10.sketch_text.stroke-99"),sQuery(id+"F4.wireOp",EDGE,"E10.sketch_text.stroke-100"),sQuery(id+"F4.wireOp",EDGE,"E10.sketch_text.stroke-101"),sQuery(id+"F4.wireOp",EDGE,"E10.sketch_text.stroke-102"),sQuery(id+"F4.wireOp",EDGE,"E10.sketch_text.stroke-103"),sQuery(id+"F4.wireOp",EDGE,"E10.sketch_text.stroke-104")])],"isStart":false});
            var Q117;
            Q117=makeQuery(id+"F5.opExtrude","SWEPT_FACE",FACE,{"disambiguationData":[OSD([sQuery(id+"F4.wireOp",EDGE,"E10.sketch_text.stroke-33")])]});
            var Q118;
            Q118=makeQuery(id+"F5.opExtrude","SWEPT_FACE",FACE,{"disambiguationData":[OSD([sQuery(id+"F4.wireOp",EDGE,"E10.sketch_text.stroke-93")])]});
            var Q119;
            Q119=makeQuery(id+"F5.opExtrude","SWEPT_FACE",FACE,{"disambiguationData":[OSD([sQuery(id+"F4.wireOp",EDGE,"E10.sketch_text.stroke-34")])]});
            var Q120;
            Q120=makeQuery(id+"F5.opExtrude","SWEPT_FACE",FACE,{"disambiguationData":[OSD([sQuery(id+"F4.wireOp",EDGE,"E10.sketch_text.stroke-152")])]});
            var Q121;
            Q121=makeQuery(id+"F5.opExtrude","SWEPT_FACE",FACE,{"disambiguationData":[OSD([sQuery(id+"F4.wireOp",EDGE,"E10.sketch_text.stroke-51")])]});
            var Q122;
            Q122=makeQuery(id+"F5.opExtrude","SWEPT_FACE",FACE,{"disambiguationData":[OSD([sQuery(id+"F4.wireOp",EDGE,"E10.sketch_text.stroke-6")])]});
            var Q123;
            Q123=makeQuery(id+"F5.opExtrude","SWEPT_FACE",FACE,{"disambiguationData":[OSD([sQuery(id+"F4.wireOp",EDGE,"E10.sketch_text.stroke-7")])]});
            var Q124;
            Q124=makeQuery(id+"F5.opExtrude","SWEPT_FACE",FACE,{"disambiguationData":[OSD([sQuery(id+"F4.wireOp",EDGE,"E10.sketch_text.stroke-156")])]});
            var Q125;
            Q125=makeQuery(id+"F5.opExtrude","SWEPT_FACE",FACE,{"disambiguationData":[OSD([sQuery(id+"F4.wireOp",EDGE,"E10.sketch_text.stroke-112")])]});
            var Q126;
            Q126=makeQuery(id+"F5.boolean.opBoolean","SPLIT",FACE,{"disambiguationData":[TD([makeQuery(id+"F5.opExtrude","SWEPT_FACE",FACE,{"disambiguationData":[OSD([sQuery(id+"F4.wireOp",EDGE,"E10.sketch_text.stroke-182")])]})])],"derivedFrom":makeQuery(id+"F1.opExtrude","CAP_FACE",FACE,{"disambiguationData":[OSD([sQuery(id+"F0.wireOp",EDGE,"E0.bottom"),sQuery(id+"F0.wireOp",EDGE,"E0.top"),sQuery(id+"F0.wireOp",EDGE,"E0.left"),sQuery(id+"F0.wireOp",EDGE,"E0.right"),sQuery(id+"F0.wireOp",EDGE,"E1"),sQuery(id+"F0.wireOp",EDGE,"E7.MirrorC"),sQuery(id+"F0.wireOp",EDGE,"E8.MirrorC"),sQuery(id+"F0.wireOp",EDGE,"E9.MirrorC")])],"isStart":true})});
            var Q127;
            Q127=makeQuery(id+"F5.opExtrude","SWEPT_FACE",FACE,{"disambiguationData":[OSD([sQuery(id+"F4.wireOp",EDGE,"E10.sketch_text.stroke-96")])]});
            var Q128;
            Q128=makeQuery(id+"F5.opExtrude","SWEPT_FACE",FACE,{"disambiguationData":[OSD([sQuery(id+"F4.wireOp",EDGE,"E10.sketch_text.stroke-114")])]});
            var Q129;
            Q129=makeQuery(id+"F5.opExtrude","SWEPT_FACE",FACE,{"disambiguationData":[OSD([sQuery(id+"F4.wireOp",EDGE,"E10.sketch_text.stroke-39")])]});
            var Q130;
            Q130=makeQuery(id+"F5.opExtrude","SWEPT_FACE",FACE,{"disambiguationData":[OSD([sQuery(id+"F4.wireOp",EDGE,"E10.sketch_text.stroke-13")])]});
            var Q131;
            Q131=makeQuery(id+"F5.opExtrude","SWEPT_FACE",FACE,{"disambiguationData":[OSD([sQuery(id+"F4.wireOp",EDGE,"E10.sketch_text.stroke-115")])]});
            var Q132;
            Q132=makeQuery(id+"F5.opExtrude","SWEPT_FACE",FACE,{"disambiguationData":[OSD([sQuery(id+"F4.wireOp",EDGE,"E10.sketch_text.stroke-56")])]});
            var Q133;
            Q133=makeQuery(id+"F5.opExtrude","SWEPT_FACE",FACE,{"disambiguationData":[OSD([sQuery(id+"F4.wireOp",EDGE,"E10.sketch_text.stroke-144")])]});
            var Q134;
            Q134=makeQuery(id+"F5.opExtrude","SWEPT_FACE",FACE,{"disambiguationData":[OSD([sQuery(id+"F4.wireOp",EDGE,"E10.sketch_text.stroke-190")])]});
            var Q135;
            Q135=makeQuery(id+"F5.opExtrude","SWEPT_FACE",FACE,{"disambiguationData":[OSD([sQuery(id+"F4.wireOp",EDGE,"E10.sketch_text.stroke-116")])]});
            var Q136;
            Q136=makeQuery(id+"F5.opExtrude","SWEPT_FACE",FACE,{"disambiguationData":[OSD([sQuery(id+"F4.wireOp",EDGE,"E10.sketch_text.stroke-41")])]});
            var Q137;
            Q137=makeQuery(id+"F5.opExtrude","SWEPT_FACE",FACE,{"disambiguationData":[OSD([sQuery(id+"F4.wireOp",EDGE,"E10.sketch_text.stroke-161")])]});
            var Q138;
            Q138=makeQuery(id+"F5.opExtrude","SWEPT_FACE",FACE,{"disambiguationData":[OSD([sQuery(id+"F4.wireOp",EDGE,"E10.sketch_text.stroke-146")])]});
            var Q139;
            Q139=makeQuery(id+"F5.opExtrude","SWEPT_FACE",FACE,{"disambiguationData":[OSD([sQuery(id+"F4.wireOp",EDGE,"E10.sketch_text.stroke-58")])]});
            var Q140;
            Q140=makeQuery(id+"F5.opExtrude","SWEPT_FACE",FACE,{"disambiguationData":[OSD([sQuery(id+"F4.wireOp",EDGE,"E10.sketch_text.stroke-105")])]});
            var Q141;
            Q141=makeQuery(id+"F5.opExtrude","SWEPT_FACE",FACE,{"disambiguationData":[OSD([sQuery(id+"F4.wireOp",EDGE,"E10.sketch_text.stroke-177")])]});
            var Q142;
            Q142=makeQuery(id+"F5.opExtrude","SWEPT_FACE",FACE,{"disambiguationData":[OSD([sQuery(id+"F4.wireOp",EDGE,"E10.sketch_text.stroke-77")])]});
            var Q143;
            Q143=makeQuery(id+"F5.opExtrude","SWEPT_FACE",FACE,{"disambiguationData":[OSD([sQuery(id+"F4.wireOp",EDGE,"E10.sketch_text.stroke-138")])]});
            var Q144;
            Q144=makeQuery(id+"F5.opExtrude","SWEPT_FACE",FACE,{"disambiguationData":[OSD([sQuery(id+"F4.wireOp",EDGE,"E10.sketch_text.stroke-111")])]});
            var Q145;
            Q145=makeQuery(id+"F5.opExtrude","SWEPT_FACE",FACE,{"disambiguationData":[OSD([sQuery(id+"F4.wireOp",EDGE,"E10.sketch_text.stroke-53")])]});
            var Q146;
            Q146=makeQuery(id+"F5.opExtrude","SWEPT_FACE",FACE,{"disambiguationData":[OSD([sQuery(id+"F4.wireOp",EDGE,"E10.sketch_text.stroke-141")])]});
            var Q147;
            Q147=makeQuery(id+"F5.opExtrude","SWEPT_FACE",FACE,{"disambiguationData":[OSD([sQuery(id+"F4.wireOp",EDGE,"E10.sketch_text.stroke-157")])]});
            var Q148;
            Q148=makeQuery(id+"F5.opExtrude","SWEPT_FACE",FACE,{"disambiguationData":[OSD([sQuery(id+"F4.wireOp",EDGE,"E10.sketch_text.stroke-64")])]});
            var Q149;
            Q149=makeQuery(id+"F5.boolean.opBoolean","SPLIT",FACE,{"disambiguationData":[TD([makeQuery(id+"F5.opExtrude","SWEPT_FACE",FACE,{"disambiguationData":[OSD([sQuery(id+"F4.wireOp",EDGE,"E10.sketch_text.stroke-53")])]})])],"derivedFrom":makeQuery(id+"F1.opExtrude","CAP_FACE",FACE,{"disambiguationData":[OSD([sQuery(id+"F0.wireOp",EDGE,"E0.bottom"),sQuery(id+"F0.wireOp",EDGE,"E0.top"),sQuery(id+"F0.wireOp",EDGE,"E0.left"),sQuery(id+"F0.wireOp",EDGE,"E0.right"),sQuery(id+"F0.wireOp",EDGE,"E1"),sQuery(id+"F0.wireOp",EDGE,"E7.MirrorC"),sQuery(id+"F0.wireOp",EDGE,"E8.MirrorC"),sQuery(id+"F0.wireOp",EDGE,"E9.MirrorC")])],"isStart":true})});
            var Q150;
            Q150=makeQuery(id+"F5.opExtrude","SWEPT_FACE",FACE,{"disambiguationData":[OSD([sQuery(id+"F4.wireOp",EDGE,"E10.sketch_text.stroke-36")])]});
            var Q151;
            Q151=makeQuery(id+"F5.opExtrude","SWEPT_FACE",FACE,{"disambiguationData":[OSD([sQuery(id+"F4.wireOp",EDGE,"E10.sketch_text.stroke-22")])]});
            var Q152;
            Q152=makeQuery(id+"F5.boolean.opBoolean","SPLIT",FACE,{"disambiguationData":[TD([makeQuery(id+"F5.opExtrude","SWEPT_FACE",FACE,{"disambiguationData":[OSD([sQuery(id+"F4.wireOp",EDGE,"E10.sketch_text.stroke-119")])]})])],"derivedFrom":makeQuery(id+"F1.opExtrude","CAP_FACE",FACE,{"disambiguationData":[OSD([sQuery(id+"F0.wireOp",EDGE,"E0.bottom"),sQuery(id+"F0.wireOp",EDGE,"E0.top"),sQuery(id+"F0.wireOp",EDGE,"E0.left"),sQuery(id+"F0.wireOp",EDGE,"E0.right"),sQuery(id+"F0.wireOp",EDGE,"E1"),sQuery(id+"F0.wireOp",EDGE,"E7.MirrorC"),sQuery(id+"F0.wireOp",EDGE,"E8.MirrorC"),sQuery(id+"F0.wireOp",EDGE,"E9.MirrorC")])],"isStart":true})});
            var Q153;
            Q153=makeQuery(id+"F5.boolean.opBoolean","SPLIT",FACE,{"disambiguationData":[TD([makeQuery(id+"F5.opExtrude","SWEPT_FACE",FACE,{"disambiguationData":[OSD([sQuery(id+"F4.wireOp",EDGE,"E10.sketch_text.stroke-158")])]})])],"derivedFrom":makeQuery(id+"F1.opExtrude","CAP_FACE",FACE,{"disambiguationData":[OSD([sQuery(id+"F0.wireOp",EDGE,"E0.bottom"),sQuery(id+"F0.wireOp",EDGE,"E0.top"),sQuery(id+"F0.wireOp",EDGE,"E0.left"),sQuery(id+"F0.wireOp",EDGE,"E0.right"),sQuery(id+"F0.wireOp",EDGE,"E1"),sQuery(id+"F0.wireOp",EDGE,"E7.MirrorC"),sQuery(id+"F0.wireOp",EDGE,"E8.MirrorC"),sQuery(id+"F0.wireOp",EDGE,"E9.MirrorC")])],"isStart":true})});
            var Q154;
            Q154=makeQuery(id+"F5.opExtrude","SWEPT_FACE",FACE,{"disambiguationData":[OSD([sQuery(id+"F4.wireOp",EDGE,"E10.sketch_text.stroke-9")])]});
            var Q155;
            Q155=makeQuery(id+"F5.opExtrude","SWEPT_FACE",FACE,{"disambiguationData":[OSD([sQuery(id+"F4.wireOp",EDGE,"E10.sketch_text.stroke-167")])]});
            var Q156;
            Q156=makeQuery(id+"F5.opExtrude","SWEPT_FACE",FACE,{"disambiguationData":[OSD([sQuery(id+"F4.wireOp",EDGE,"E10.sketch_text.stroke-95")])]});
            var Q157;
            Q157=makeQuery(id+"F5.opExtrude","SWEPT_FACE",FACE,{"disambiguationData":[OSD([sQuery(id+"F4.wireOp",EDGE,"E10.sketch_text.stroke-184")])]});
            var Q158;
            Q158=makeQuery(id+"F5.opExtrude","SWEPT_FACE",FACE,{"disambiguationData":[OSD([sQuery(id+"F4.wireOp",EDGE,"E10.sketch_text.stroke-84")])]});
            var Q159;
            Q159=makeQuery(id+"F5.opExtrude","SWEPT_FACE",FACE,{"disambiguationData":[OSD([sQuery(id+"F4.wireOp",EDGE,"E10.sketch_text.stroke-68")])]});
            var Q160;
            Q160=makeQuery(id+"F5.opExtrude","SWEPT_FACE",FACE,{"disambiguationData":[OSD([sQuery(id+"F4.wireOp",EDGE,"E10.sketch_text.stroke-143")])]});
            var Q161;
            Q161=makeQuery(id+"F5.opExtrude","SWEPT_FACE",FACE,{"disambiguationData":[OSD([sQuery(id+"F4.wireOp",EDGE,"E10.sketch_text.stroke-189")])]});
            var Q162;
            Q162=makeQuery(id+"F5.opExtrude","CAP_FACE",FACE,{"disambiguationData":[OSD([sQuery(id+"F4.wireOp",EDGE,"E10.sketch_text.stroke-13"),sQuery(id+"F4.wireOp",EDGE,"E10.sketch_text.stroke-14"),sQuery(id+"F4.wireOp",EDGE,"E10.sketch_text.stroke-15"),sQuery(id+"F4.wireOp",EDGE,"E10.sketch_text.stroke-16"),sQuery(id+"F4.wireOp",EDGE,"E10.sketch_text.stroke-17"),sQuery(id+"F4.wireOp",EDGE,"E10.sketch_text.stroke-18"),sQuery(id+"F4.wireOp",EDGE,"E10.sketch_text.stroke-19"),sQuery(id+"F4.wireOp",EDGE,"E10.sketch_text.stroke-20")])],"isStart":false});
            var Q163;
            Q163=makeQuery(id+"F5.opExtrude","SWEPT_FACE",FACE,{"disambiguationData":[OSD([sQuery(id+"F4.wireOp",EDGE,"E10.sketch_text.stroke-57")])]});
            var Q164;
            Q164=makeQuery(id+"F5.opExtrude","SWEPT_FACE",FACE,{"disambiguationData":[OSD([sQuery(id+"F4.wireOp",EDGE,"E10.sketch_text.stroke-29")])]});
            var Q165;
            Q165=makeQuery(id+"F5.opExtrude","SWEPT_FACE",FACE,{"disambiguationData":[OSD([sQuery(id+"F4.wireOp",EDGE,"E10.sketch_text.stroke-60")])]});
            var Q166;
            Q166=makeQuery(id+"F5.opExtrude","SWEPT_FACE",FACE,{"disambiguationData":[OSD([sQuery(id+"F4.wireOp",EDGE,"E10.sketch_text.stroke-148")])]});
            var Q167;
            Q167=makeQuery(id+"F5.opExtrude","SWEPT_FACE",FACE,{"disambiguationData":[OSD([sQuery(id+"F4.wireOp",EDGE,"E10.sketch_text.stroke-75")])]});
            var Q168;
            Q168=makeQuery(id+"F5.opExtrude","SWEPT_FACE",FACE,{"disambiguationData":[OSD([sQuery(id+"F4.wireOp",EDGE,"E10.sketch_text.stroke-91")])]});
            var Q169;
            Q169=makeQuery(id+"F5.opExtrude","SWEPT_FACE",FACE,{"disambiguationData":[OSD([sQuery(id+"F4.wireOp",EDGE,"E10.sketch_text.stroke-78")])]});
            var Q170;
            Q170=makeQuery(id+"F5.opExtrude","SWEPT_FACE",FACE,{"disambiguationData":[OSD([sQuery(id+"F4.wireOp",EDGE,"E10.sketch_text.stroke-62")])]});
            var Q171;
            Q171=makeQuery(id+"F5.opExtrude","SWEPT_FACE",FACE,{"disambiguationData":[OSD([sQuery(id+"F4.wireOp",EDGE,"E10.sketch_text.stroke-182")])]});
            var Q172;
            Q172=makeQuery(id+"F5.opExtrude","SWEPT_FACE",FACE,{"disambiguationData":[OSD([sQuery(id+"F4.wireOp",EDGE,"E10.sketch_text.stroke-11")])]});
            var Q173;
            Q173=makeQuery(id+"F5.opExtrude","SWEPT_FACE",FACE,{"disambiguationData":[OSD([sQuery(id+"F4.wireOp",EDGE,"E10.sketch_text.stroke-97")])]});
            var Q174;
            Q174=makeQuery(id+"F5.opExtrude","SWEPT_FACE",FACE,{"disambiguationData":[OSD([sQuery(id+"F4.wireOp",EDGE,"E10.sketch_text.stroke-23")])]});
            var Q175;
            Q175=makeQuery(id+"F5.opExtrude","SWEPT_FACE",FACE,{"disambiguationData":[OSD([sQuery(id+"F4.wireOp",EDGE,"E10.sketch_text.stroke-80")])]});
            var Q176;
            Q176=makeQuery(id+"F5.boolean.opBoolean","SPLIT",FACE,{"disambiguationData":[TD([makeQuery(id+"F5.opExtrude","SWEPT_FACE",FACE,{"disambiguationData":[OSD([sQuery(id+"F4.wireOp",EDGE,"E10.sketch_text.stroke-99")])]})])],"derivedFrom":makeQuery(id+"F1.opExtrude","CAP_FACE",FACE,{"disambiguationData":[OSD([sQuery(id+"F0.wireOp",EDGE,"E0.bottom"),sQuery(id+"F0.wireOp",EDGE,"E0.top"),sQuery(id+"F0.wireOp",EDGE,"E0.left"),sQuery(id+"F0.wireOp",EDGE,"E0.right"),sQuery(id+"F0.wireOp",EDGE,"E1"),sQuery(id+"F0.wireOp",EDGE,"E7.MirrorC"),sQuery(id+"F0.wireOp",EDGE,"E8.MirrorC"),sQuery(id+"F0.wireOp",EDGE,"E9.MirrorC")])],"isStart":true})});
            var Q177;
            Q177=makeQuery(id+"F5.opExtrude","SWEPT_FACE",FACE,{"disambiguationData":[OSD([sQuery(id+"F4.wireOp",EDGE,"E10.sketch_text.stroke-168")])]});
            var Q178;
            Q178=makeQuery(id+"F5.opExtrude","SWEPT_FACE",FACE,{"disambiguationData":[OSD([sQuery(id+"F4.wireOp",EDGE,"E10.sketch_text.stroke-188")])]});
            var Q179;
            Q179=makeQuery(id+"F5.opExtrude","SWEPT_FACE",FACE,{"disambiguationData":[OSD([sQuery(id+"F4.wireOp",EDGE,"E10.sketch_text.stroke-129")])]});
            var Q180;
            Q180=makeQuery(id+"F5.opExtrude","SWEPT_FACE",FACE,{"disambiguationData":[OSD([sQuery(id+"F4.wireOp",EDGE,"E10.sketch_text.stroke-27")])]});
            var Q181;
            Q181=makeQuery(id+"F5.opExtrude","SWEPT_FACE",FACE,{"disambiguationData":[OSD([sQuery(id+"F4.wireOp",EDGE,"E10.sketch_text.stroke-175")])]});
            var Q182;
            Q182=makeQuery(id+"F5.opExtrude","SWEPT_FACE",FACE,{"disambiguationData":[OSD([sQuery(id+"F4.wireOp",EDGE,"E10.sketch_text.stroke-42")])]});
            var Q183;
            Q183=makeQuery(id+"F5.opExtrude","SWEPT_FACE",FACE,{"disambiguationData":[OSD([sQuery(id+"F4.wireOp",EDGE,"E10.sketch_text.stroke-118")])]});
            var Q184;
            Q184=makeQuery(id+"F5.opExtrude","SWEPT_FACE",FACE,{"disambiguationData":[OSD([sQuery(id+"F4.wireOp",EDGE,"E10.sketch_text.stroke-151")])]});
            var Q185;
            Q185=makeQuery(id+"F5.opExtrude","SWEPT_FACE",FACE,{"disambiguationData":[OSD([sQuery(id+"F4.wireOp",EDGE,"E10.sketch_text.stroke-137")])]});
            var Q186;
            Q186=makeQuery(id+"F5.opExtrude","SWEPT_FACE",FACE,{"disambiguationData":[OSD([sQuery(id+"F4.wireOp",EDGE,"E10.sketch_text.stroke-83")])]});
            var Q187;
            Q187=makeQuery(id+"F5.boolean.opBoolean","SPLIT",FACE,{"disambiguationData":[TD([makeQuery(id+"F5.opExtrude","SWEPT_FACE",FACE,{"disambiguationData":[OSD([sQuery(id+"F4.wireOp",EDGE,"E10.sketch_text.stroke-90")])]})])],"derivedFrom":makeQuery(id+"F1.opExtrude","CAP_FACE",FACE,{"disambiguationData":[OSD([sQuery(id+"F0.wireOp",EDGE,"E0.bottom"),sQuery(id+"F0.wireOp",EDGE,"E0.top"),sQuery(id+"F0.wireOp",EDGE,"E0.left"),sQuery(id+"F0.wireOp",EDGE,"E0.right"),sQuery(id+"F0.wireOp",EDGE,"E1"),sQuery(id+"F0.wireOp",EDGE,"E7.MirrorC"),sQuery(id+"F0.wireOp",EDGE,"E8.MirrorC"),sQuery(id+"F0.wireOp",EDGE,"E9.MirrorC")])],"isStart":true})});
            var Q188;
            Q188=makeQuery(id+"F5.opExtrude","SWEPT_FACE",FACE,{"disambiguationData":[OSD([sQuery(id+"F4.wireOp",EDGE,"E10.sketch_text.stroke-139")])]});
            var Q189;
            Q189=makeQuery(id+"F5.opExtrude","SWEPT_FACE",FACE,{"disambiguationData":[OSD([sQuery(id+"F4.wireOp",EDGE,"E10.sketch_text.stroke-70")])]});
            var Q190;
            Q190=makeQuery(id+"F5.opExtrude","SWEPT_FACE",FACE,{"disambiguationData":[OSD([sQuery(id+"F4.wireOp",EDGE,"E10.sketch_text.stroke-160")])]});
            var Q191;
            Q191=makeQuery(id+"F5.opExtrude","SWEPT_FACE",FACE,{"disambiguationData":[OSD([sQuery(id+"F4.wireOp",EDGE,"E10.sketch_text.stroke-71")])]});
            var Q192;
            Q192=makeQuery(id+"F5.opExtrude","SWEPT_FACE",FACE,{"disambiguationData":[OSD([sQuery(id+"F4.wireOp",EDGE,"E10.sketch_text.stroke-117")])]});
            var Q193;
            Q193=makeQuery(id+"F5.opExtrude","SWEPT_FACE",FACE,{"disambiguationData":[OSD([sQuery(id+"F4.wireOp",EDGE,"E10.sketch_text.stroke-147")])]});
            var Q194;
            Q194=makeQuery(id+"F5.opExtrude","SWEPT_FACE",FACE,{"disambiguationData":[OSD([sQuery(id+"F4.wireOp",EDGE,"E10.sketch_text.stroke-164")])]});
            var Q195;
            Q195=makeQuery(id+"F5.opExtrude","SWEPT_FACE",FACE,{"disambiguationData":[OSD([sQuery(id+"F4.wireOp",EDGE,"E10.sketch_text.stroke-61")])]});
            var Q196;
            Q196=makeQuery(id+"F5.opExtrude","SWEPT_FACE",FACE,{"disambiguationData":[OSD([sQuery(id+"F4.wireOp",EDGE,"E10.sketch_text.stroke-19")])]});
            var Q197;
            Q197=makeQuery(id+"F5.opExtrude","SWEPT_FACE",FACE,{"disambiguationData":[OSD([sQuery(id+"F4.wireOp",EDGE,"E10.sketch_text.stroke-35")])]});
            var Q198;
            Q198=makeQuery(id+"F5.opExtrude","SWEPT_FACE",FACE,{"disambiguationData":[OSD([sQuery(id+"F4.wireOp",EDGE,"E10.sketch_text.stroke-140")])]});
            var Q199;
            Q199=makeQuery(id+"F5.opExtrude","SWEPT_FACE",FACE,{"disambiguationData":[OSD([sQuery(id+"F4.wireOp",EDGE,"E10.sketch_text.stroke-20")])]});
            var Q200;
            Q200=makeQuery(id+"F5.opExtrude","SWEPT_FACE",FACE,{"disambiguationData":[OSD([sQuery(id+"F4.wireOp",EDGE,"E10.sketch_text.stroke-16")])]});
            var Q201;
            Q201=makeQuery(id+"F5.opExtrude","SWEPT_FACE",FACE,{"disambiguationData":[OSD([sQuery(id+"F4.wireOp",EDGE,"E10.sketch_text.stroke-18")])]});
            var Q202;
            Q202=makeQuery(id+"F5.opExtrude","SWEPT_FACE",FACE,{"disambiguationData":[OSD([sQuery(id+"F4.wireOp",EDGE,"E10.sketch_text.stroke-17")])]});
            var Q203;
            Q203=qCreatedBy(makeId("Right.planeOp"),FACE);
            mirror(context, id + "F6", {"operationType" : NewBodyOperationType.ADD, "entities" : qUnion([Q0]), "faces" : qUnion([Q1, Q2, Q3, Q4, Q5, Q6, Q7, Q8, Q9, Q10, Q11, Q12, Q13, Q14, Q15, Q16, Q17, Q18, Q19, Q20, Q21, Q22, Q23, Q24, Q25, Q26, Q27, Q28, Q29, Q30, Q31, Q32, Q33, Q34, Q35, Q36, Q37, Q38, Q39, Q40, Q41, Q42, Q43, Q44, Q45, Q46, Q47, Q48, Q49, Q50, Q51, Q52, Q53, Q54, Q55, Q56, Q57, Q58, Q59, Q60, Q61, Q62, Q63, Q64, Q65, Q66, Q67, Q68, Q69, Q70, Q71, Q72, Q73, Q74, Q75, Q76, Q77, Q78, Q79, Q80, Q81, Q82, Q83, Q84, Q85, Q86, Q87, Q88, Q89, Q90, Q91, Q92, Q93, Q94, Q95, Q96, Q97, Q98, Q99, Q100, Q101, Q102, Q103, Q104, Q105, Q106, Q107, Q108, Q109, Q110, Q111, Q112, Q113, Q114, Q115, Q116, Q117, Q118, Q119, Q120, Q121, Q122, Q123, Q124, Q125, Q126, Q127, Q128, Q129, Q130, Q131, Q132, Q133, Q134, Q135, Q136, Q137, Q138, Q139, Q140, Q141, Q142, Q143, Q144, Q145, Q146, Q147, Q148, Q149, Q150, Q151, Q152, Q153, Q154, Q155, Q156, Q157, Q158, Q159, Q160, Q161, Q162, Q163, Q164, Q165, Q166, Q167, Q168, Q169, Q170, Q171, Q172, Q173, Q174, Q175, Q176, Q177, Q178, Q179, Q180, Q181, Q182, Q183, Q184, Q185, Q186, Q187, Q188, Q189, Q190, Q191, Q192, Q193, Q194, Q195, Q196, Q197, Q198, Q199, Q200, Q201, Q202]), "mirrorPlane" : qUnion([Q203])});
        }
    });
